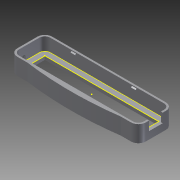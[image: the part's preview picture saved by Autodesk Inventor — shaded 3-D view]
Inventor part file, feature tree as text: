
AUTODESK INVENTOR PART (.ipt)
format: ipt  version: 2014 (Build 180170000, 170)  size: 259,584 bytes
history: native  units: mm
features: sketch x9, extrude x8, chamfer x4, fillet x1
ambient origin geometry x8: Origin, YZ Plane, XZ Plane, XY Plane, X Axis, Y Axis, Z Axis, Center Point
bodies: Solid1 (feature_tree)
feature tree (22):
  extrude  "Extrusion1"  Depth=38.0mm
  extrude  "Extrusion2"  Depth=19.0mm
  extrude  "Extrusion3"  Depth=8.0mm
  extrude  "Extrusion4"  Depth=8.0mm
  chamfer  "Chamfer1"  Distance=18.0mm
  chamfer  "Chamfer3"  Distance=14.0mm
  chamfer  "Chamfer4"  Distance=14.0mm
  chamfer  "Chamfer5"  Distance=38.0mm
  extrude  "Extrusion5"  Depth=5.0mm
  extrude  "Extrusion6"  Depth=5.0mm
  extrude  "Extrusion8"  Depth=38.0mm
  extrude  "Extrusion9"  Depth=1.0mm
  fillet  "Fillet1"  Radius=1.0mm
  sketch  "Sketch10"  dims[d16=7.5mm d17=14.0mm d18=0.0mm d19=38.0mm d20=5.0mm d21=5.0mm d22=38.0mm d23=1.0mm d24=1.0mm d25=0.0mm d26=0.0mm d28=1.0mm d29=0.0mm d30=5.0mm d31=5.0mm d33=1.0mm d34=0.0mm d36=13.0mm d37=0.0mm d38=1.0mm d39=1.0mm d40=45.0deg d44=1.0mm d45=1.0mm d46=45.0deg d47=1.0mm d48=1.0mm d49=45.0deg d50=1.0mm d51=1.0mm d52=45.0deg d53=10.0mm d54=5.0mm d55=11.0mm d56=0.0mm d57=0.0mm d58=0.0mm d59=66.0mm d60=74.0mm d63=2.0mm d64=18.0mm d65=18.0mm d66=5.5mm d67=30.0mm d68=30.0mm d69=10.0mm d70=0.0mm d71=3.0mm d72=4.0mm d73=4.0mm d74=4.0mm d75=10.0mm d76=0.0mm d77=2.0mm]
  sketch  "Sketch1"  dims[d0=140.0mm d1=38.0mm]
  sketch  "Sketch2"  dims[d2=70.0mm d3=19.0mm]
  sketch  "Sketch3"  dims[d4=8.0mm d5=8.0mm]
  sketch  "Sketch4"  dims[d6=8.0mm d7=8.0mm d8=18.0mm d9=0.0mm]
  sketch  "Sketch5"  dims[d10=2.0mm d11=14.0mm d12=0.0mm]
  sketch  "Sketch6"  dims[d13=6.915756mm]
  sketch  "Sketch8"  dims[d14=10.0mm]
  sketch  "Sketch9"  dims[d15=15.0mm]
